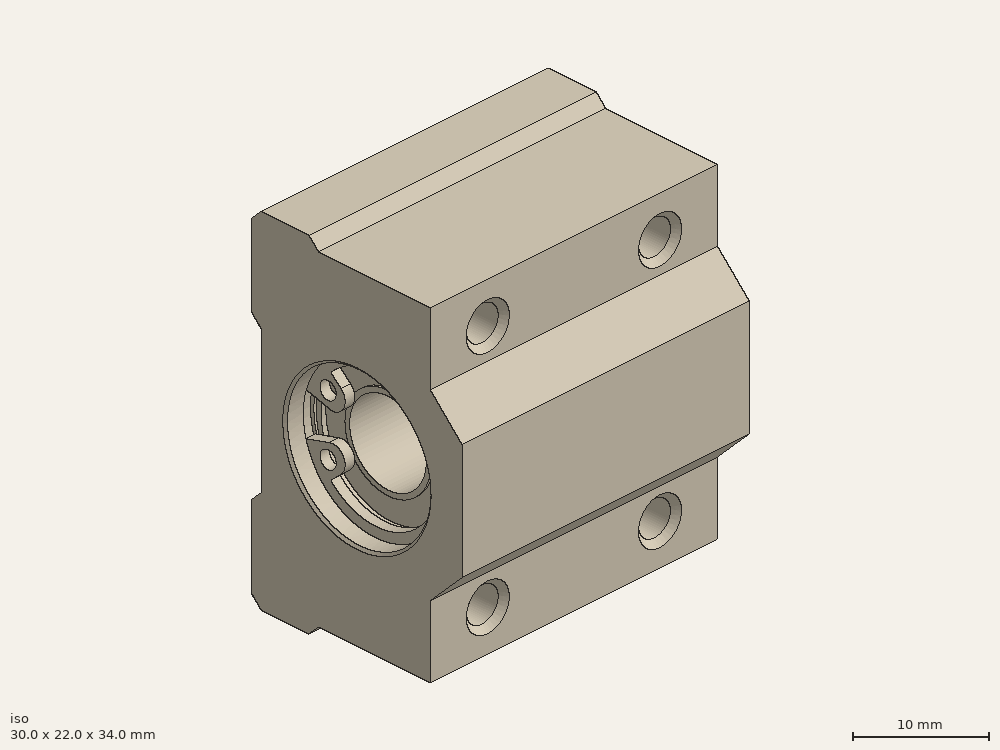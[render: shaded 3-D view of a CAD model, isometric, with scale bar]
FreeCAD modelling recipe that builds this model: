
FCSTD DOCUMENT  (FreeCAD 0.19R22960 (Git))
Label: SCS8UU
License: All rights reserved
LicenseURL: http://en.wikipedia.org/wiki/All_rights_reserved
objects: PartDesign::CoordinateSystem×3, App::DocumentObjectGroup×2, Part::Feature×1, PartDesign::FeatureBase×1, PartDesign::Body×1, App::FeaturePython×1, App::Part×1
note: 6 computed .brp shape members not serialized (recipe doc carries the construction recipe); baked Part::Feature solids carry a one-line shape summary decoded from their .brp

FEATURE [Part::Feature] Feature  label="SCS8UU Block, Linear Bearing, 8mm Shaft v005"
  shape: bbox 30 x 22.22 x 34 mm, 209 faces, 4 solids (baked)
FEATURE [PartDesign::FeatureBase] BaseFeature
  BaseFeature = -> Feature
FEATURE [PartDesign::Body] Body
  BaseFeature = -> Feature
  Group = -> [BaseFeature]
  Origin = -> Origin
  Tip = -> BaseFeature
FEATURE [App::DocumentObjectGroup] Parts
FEATURE [PartDesign::CoordinateSystem] LCS_Origin
  AttacherType = Attacher::AttachEngine3D
  MapMode = 2
  Support = -> [X_Axis001]
FEATURE [App::DocumentObjectGroup] Constraints
FEATURE [App::FeaturePython] Variables  # WARN: FeaturePython — macro-defined, semantics opaque (R4)
FEATURE [PartDesign::CoordinateSystem] MH1
  AttacherType = Attacher::AttachEngine3D
  AttachmentOffset = pos=(6,0,-4) rot=(0,0,1;0rad)
  MapMode = 1
  Placement = pos=(6,1,-5) rot=(0.57735,-0.57735,-0.57735;2.0944rad)
  Support = -> [BaseFeature]
FEATURE [PartDesign::CoordinateSystem] Rail_MH
  AttacherType = Attacher::AttachEngine3D
  MapMode = 11
  Placement = pos=(26.75,-10,-17) rot=(0.707107,0,0.707107;3.14159rad)
  Support = -> [BaseFeature]
FEATURE [App::Part] Model
  Configuration = 0
  Group = -> [LCS_Origin,Constraints,Variables,Feature,Body,MH1,Rail_MH]
  Origin = -> Origin001
  Type = Assembly4 Model
